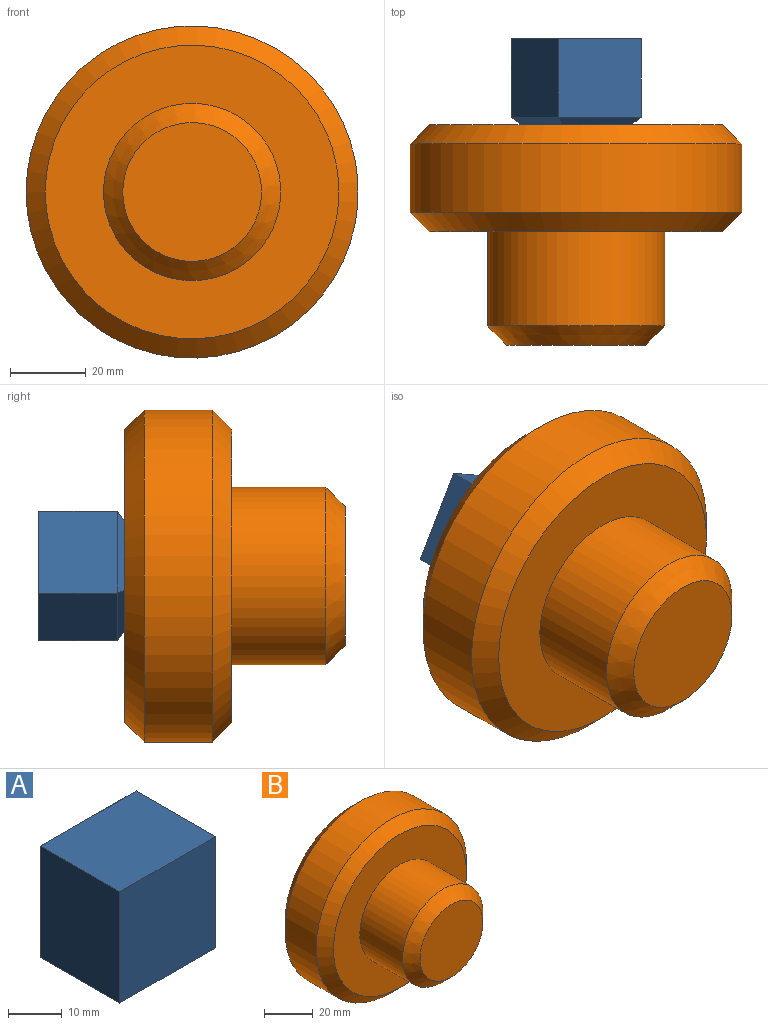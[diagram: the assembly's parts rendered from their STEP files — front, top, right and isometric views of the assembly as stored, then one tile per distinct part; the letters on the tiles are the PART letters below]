
ASSEMBLY  parts=2 mates=1
PART A: 10 faces, bbox 25x22.7x25.2 mm
  f0: plane 25x20.72mm, normal (0,0,1), area 518.1mm2, adj f1,f4,f5,f7
  f1: plane 25.25x25mm, normal (0,-1,0), area 631.2mm2, adj f0,f2,f4,f5
  f2: plane 25x20.72mm, normal (0,0,-1), area 518.1mm2, adj f1,f4,f5,f8
  f3: plane 21.25x21mm, normal (0,1,0), area 446.2mm2, adj f6,f7,f8,f9
  f4: plane 25.25x20.72mm, normal (1,0,0), area 523.3mm2, adj f0,f1,f2,f9
  f5: plane 25.25x20.72mm, normal (-1,0,0), area 523.3mm2, adj f0,f1,f2,f6
  f6: plane 25.25x2mm, normal (-0.71,0.71,0), area 65.8mm2, adj f3,f5,f7,f8
  f7: plane 25x2mm, normal (0,0.71,0.71), area 65.1mm2, adj f0,f3,f6,f9
  f8: plane 25x2mm, normal (0,0.71,-0.71), area 65.1mm2, adj f2,f3,f6,f9
  f9: plane 25.25x2mm, normal (0.71,0.71,0), area 65.8mm2, adj f3,f4,f7,f8
PART B: 11 faces, bbox 87.7x58.2x87.7 mm
  f0: cylinder r=23.41mm len=46.82mm, axis (0,1,0), area 3665.8mm2, adj f4,f5
  f1: plane 36.66x36.66mm, normal (0,-1,0), area 1055.8mm2, adj f5
  f2: cylinder r=43.86mm len=87.72mm, axis (0,-1,0), area 4969.6mm2, adj f6,f7
  f3: plane 77.56x77.56mm, normal (0,1,0), area 4724.1mm2, adj f6
  f4: plane 77.56x77.56mm, normal (0,-1,0), area 3002.2mm2, adj f0,f7
  f5: cone r=18.33mm half-angle=45deg, axis (0,1,0), area 942.2mm2, adj f0,f1
  f6: cone r=43.86mm half-angle=45deg, axis (0,-1,0), area 1865.1mm2, adj f2,f3
  f7: cone r=38.78mm half-angle=45deg, axis (0,1,0), area 1865.1mm2, adj f2,f4
  f8: plane 8.5x8.5mm, normal (0,1,0), area 56.7mm2, adj f10
  f9: cone r=0mm half-angle=59deg, axis (0,-1,0), area 66.2mm2, adj f10
  f10: cylinder r=4.25mm len=17.2mm, axis (0,-1,0), area 459.3mm2, adj f8,f9
PLACE A rot(axis=(0.87,0,0.5),180deg) t=(-79.63,88.99,-19.04)mm
PLACE B rot(axis=(0,-1,0),150deg) t=(-73.93,9.51,-7.9)mm fixed
MATE revolute A.f3 <-> B.f2  axis (0,-1,0) through (-73.93,37.7,-7.9)mm
